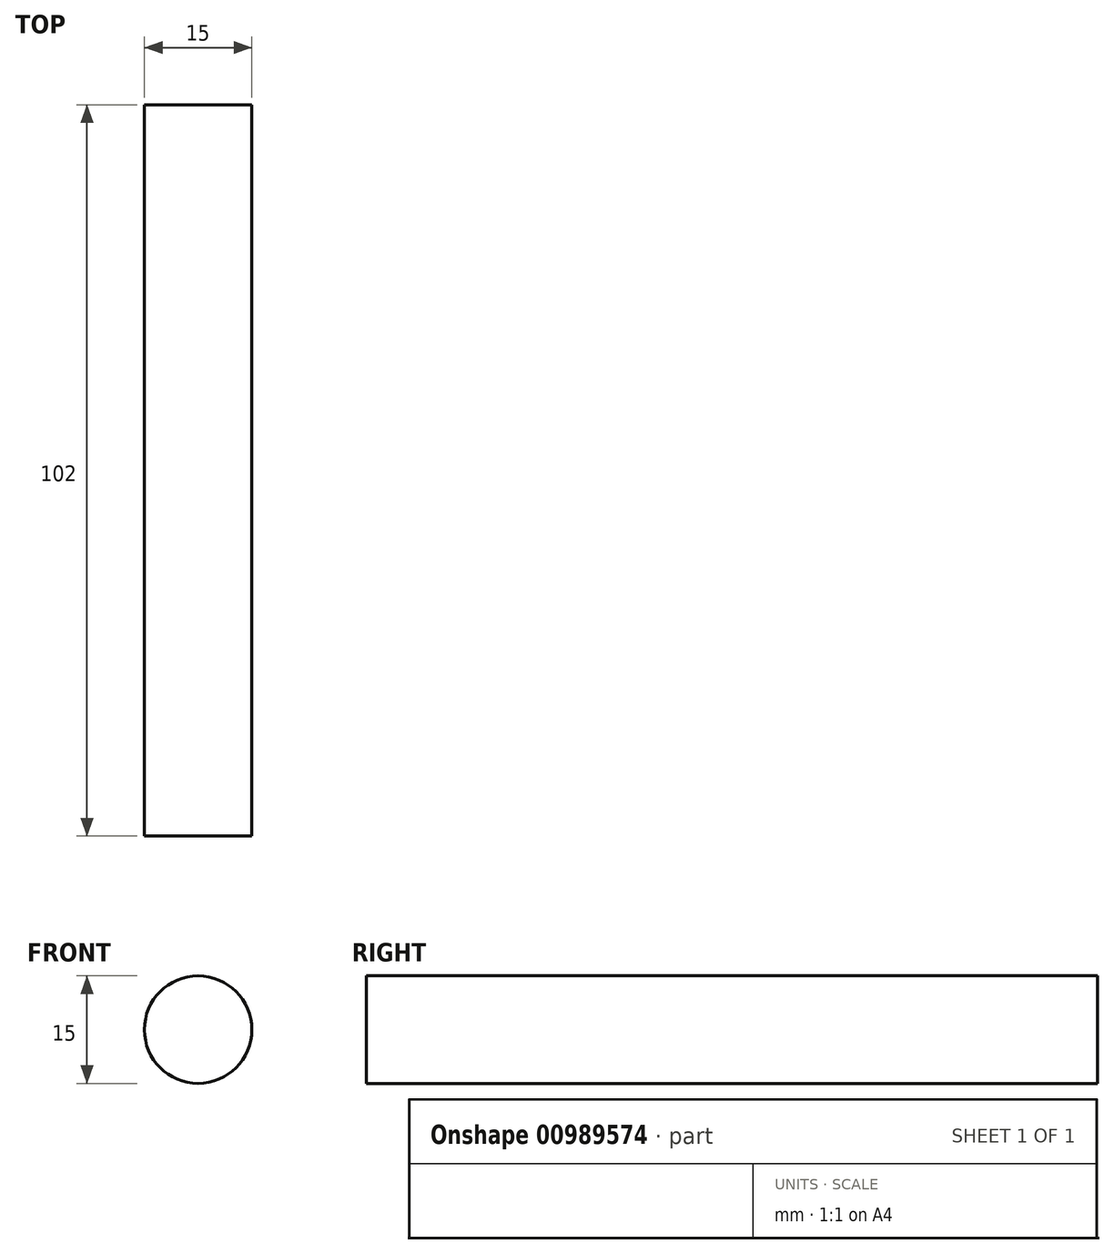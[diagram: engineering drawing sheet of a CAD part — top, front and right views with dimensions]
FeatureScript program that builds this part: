
annotation { "Feature Type Name" : "Feature", "Feature Type Description" : "" }
export const myFeature = defineFeature(function(context is Context, id is Id, definition is map)
    precondition{}
    {
        {
            var Q0;
            Q0=qCreatedBy(makeId("Front.planeOp"),FACE);
            var sketch = newSketch(context, id + "F0", { "sketchPlane" : qUnion([Q0])});
            skCircle(sketch, "E0", {"center": v(0, 0) * mm, "radius": 7.5 * mm});
            skSolve(sketch);
        }
        {
            var Q0;
            Q0 = qSketchRegion(id + "F0", true);
            extrude(context, id + "F1", {"entities" : qUnion([Q0]), "oppositeDirection" : true, "depth" : 102 * mm, "offsetDistance" : 25 * mm});
        }
    });
